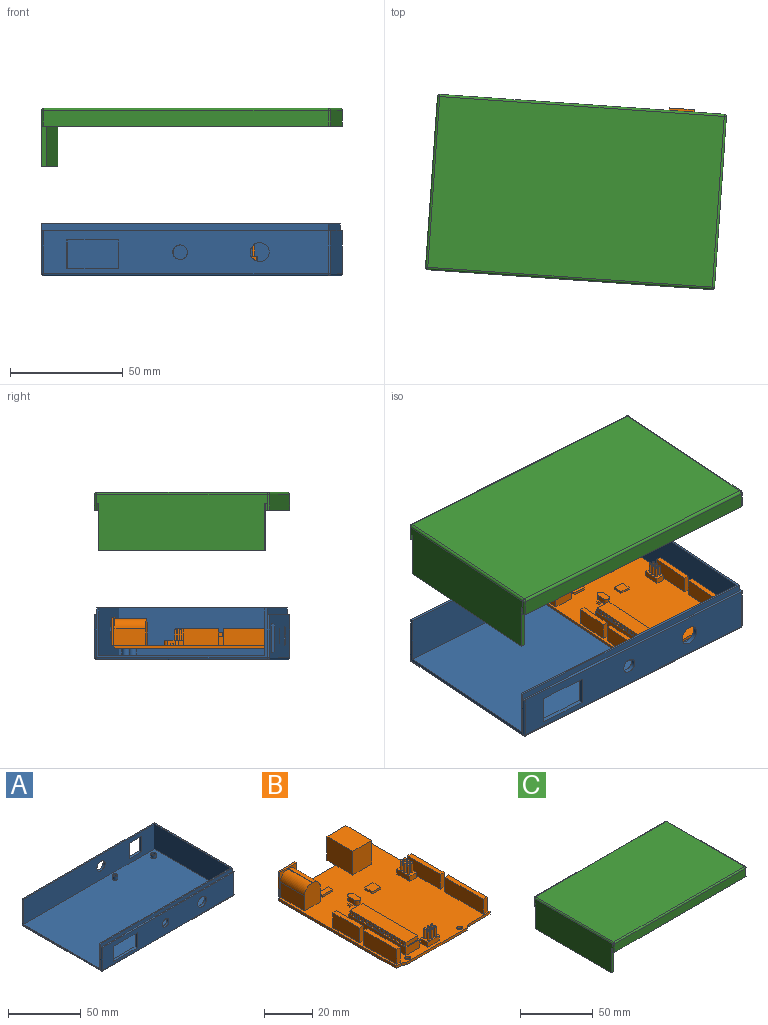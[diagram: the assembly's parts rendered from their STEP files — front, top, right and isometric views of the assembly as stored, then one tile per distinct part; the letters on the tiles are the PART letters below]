
ASSEMBLY  parts=3 mates=4
PART A: 53 faces, bbox 128.7x78x23 mm
  f0: plane 128.7x78mm, normal (0,0,1), area 350.9mm2, adj f2,f3,f7,f8,f10,f33,f34,f41
  f1: plane 126.7x21mm, normal (0,-1,0), area 2453.2mm2, adj f6,f9,f11,f28,f29,f30,f31,f32
  f2: plane 126.7x19mm, normal (0,-1,0), area 2030.7mm2, adj f0,f35,f36,f37,f38,f39,f40,f43
  f3: plane 126.7x19mm, normal (0,1,0), area 2199.8mm2, adj f0,f28,f29,f30,f31,f32,f41,f45
  f4: plane 126.7x76mm, normal (0,0,-1), area 9629.2mm2, adj f44,f45,f49,f50
  f5: plane 126.7x21mm, normal (0,1,0), area 2284.1mm2, adj f6,f9,f11,f34,f35,f36,f37,f38
  f6: plane 126.7x74mm, normal (0,0,1), area 9337.3mm2, adj f1,f5,f11,f13,f17,f21,f25,f34
  f7: plane 127.67x3mm, normal (0,1,0), area 383mm2, adj f0,f9,f33,f34
  f8: plane 127.67x3mm, normal (0,-1,0), area 383mm2, adj f0,f9,f33,f34
  f9: plane 127.67x75.88mm, normal (0,0,1), area 311.1mm2, adj f1,f5,f7,f8,f11,f33,f34
  f10: plane 76x19mm, normal (1,0,0), area 1444mm2, adj f0,f41,f43,f44
  f11: plane 74x21mm, normal (-1,0,0), area 1554mm2, adj f1,f5,f6,f9
  f12: cylinder r=1.25mm len=3mm, axis (0,0,-1), area 23.6mm2, adj f14,f15
  f13: cylinder r=1.75mm len=3.5mm, axis (0,0,-1), area 33mm2, adj f6,f14
  f14: plane 3.5x3.5mm, normal (0,0,1), area 4.7mm2, adj f12,f13
  f15: plane 2.5x2.5mm, normal (0,0,1), area 4.9mm2, adj f12
  f16: cylinder r=1.25mm len=3mm, axis (0,0,-1), area 23.6mm2, adj f18,f19
  f17: cylinder r=1.75mm len=3.5mm, axis (0,0,-1), area 33mm2, adj f6,f18
  f18: plane 3.5x3.5mm, normal (0,0,1), area 4.7mm2, adj f16,f17
  f19: plane 2.5x2.5mm, normal (0,0,1), area 4.9mm2, adj f16
  f20: cylinder r=1.25mm len=3mm, axis (0,0,-1), area 23.6mm2, adj f22,f23
  f21: cylinder r=1.75mm len=3.5mm, axis (0,0,-1), area 33mm2, adj f6,f22
  f22: plane 3.5x3.5mm, normal (0,0,1), area 4.7mm2, adj f20,f21
  f23: plane 2.5x2.5mm, normal (0,0,1), area 4.9mm2, adj f20
  f24: cylinder r=1.25mm len=3mm, axis (0,0,-1), area 23.6mm2, adj f26,f27
  f25: cylinder r=1.75mm len=3.5mm, axis (0,0,-1), area 33mm2, adj f6,f26
  f26: plane 3.5x3.5mm, normal (0,0,1), area 4.7mm2, adj f24,f25
  f27: plane 2.5x2.5mm, normal (0,0,1), area 4.9mm2, adj f24
  f28: plane 13x2mm, normal (-1,0,0), area 26mm2, adj f1,f3,f29,f31
  f29: plane 12.11x2mm, normal (0,0,1), area 24.2mm2, adj f1,f3,f28,f30
  f30: plane 13x2mm, normal (1,0,0), area 26mm2, adj f1,f3,f29,f31
  f31: plane 12.11x2mm, normal (0,0,-1), area 24.2mm2, adj f1,f3,f28,f30
  f32: cylinder r=3.99mm len=7.98mm, axis (0,1,0), area 50.2mm2, adj f1,f3
  f33: plane 75.88x3mm, normal (1,0,0), area 227.6mm2, adj f0,f7,f8,f9
  f34: plane 76x22mm, normal (-1,0,0), area 117.6mm2, adj f0,f1,f5,f6,f7,f8,f9,f46
  f35: plane 12.6x2mm, normal (1,0,0), area 25.2mm2, adj f2,f5,f36,f38
  f36: plane 22.75x2mm, normal (0,0,1), area 45.5mm2, adj f2,f5,f35,f37
  f37: plane 12.6x2mm, normal (-1,0,0), area 25.2mm2, adj f2,f5,f36,f38
  f38: plane 22.75x2mm, normal (0,0,-1), area 45.5mm2, adj f2,f5,f35,f37
  f39: cylinder r=3.25mm len=6.5mm, axis (0,-1,0), area 40.8mm2, adj f2,f5
  f40: cylinder r=4.25mm len=8.5mm, axis (0,-1,0), area 53.4mm2, adj f2,f5
  f41: cylinder r=1mm len=19mm, axis (0,0,-1), area 29.8mm2, adj f0,f3,f10,f42
  f42: sphere r=1mm, area 1.6mm2, adj f41,f44,f45
  f43: cylinder r=1mm len=19mm, axis (0,0,1), area 29.8mm2, adj f0,f2,f10,f47
  f44: cylinder r=1mm len=76mm, axis (0,1,0), area 119.4mm2, adj f4,f10,f42,f47
  f45: cylinder r=1mm len=126.7mm, axis (-1,0,0), area 199mm2, adj f3,f4,f42,f48
  f46: cylinder r=1mm len=19mm, axis (0,0,1), area 29.8mm2, adj f0,f3,f34,f48
  f47: sphere r=1mm, area 1.6mm2, adj f43,f44,f49
  f48: sphere r=1mm, area 1.6mm2, adj f45,f46,f50
  f49: cylinder r=1mm len=126.7mm, axis (1,0,0), area 199mm2, adj f2,f4,f47,f51
  f50: cylinder r=1mm len=76mm, axis (0,1,0), area 119.4mm2, adj f4,f34,f48,f51
  f51: sphere r=1mm, area 1.6mm2, adj f49,f50,f52
  f52: cylinder r=1mm len=19mm, axis (0,0,-1), area 29.8mm2, adj f0,f2,f34,f51
PART B: 244 faces, bbox 55x75.2x13.8 mm
  f0: plane 7x4mm, normal (0,0,1), area 23.3mm2, adj f194,f195,f196,f197,f226,f227,f228,f229
  f1: plane 7.5x4mm, normal (0,0,1), area 25.3mm2, adj f190,f191,f192,f193,f220,f221,f222,f223
  f2: plane 70x55mm, normal (0,0,1), area 3025.5mm2, adj f49,f50,f51,f52,f54,f55,f56,f57
  f3: plane 8.98x8.63mm, normal (0,1,0), area 52mm2, adj f179,f180,f181,f182,f183,f184,f185,f186
  f4: plane 1.5x0.4mm, normal (0,1,0), area 0.6mm2, adj f6,f46,f48,f178
  f5: plane 1.5x0.4mm, normal (0,-1,0), area 0.6mm2, adj f6,f46,f48,f178
  f6: plane 0.75x0.4mm, normal (0,0,1), area 0.3mm2, adj f4,f5,f46,f178
  f7: plane 1.5x0.4mm, normal (0,1,0), area 0.6mm2, adj f9,f46,f48,f177
  f8: plane 1.5x0.4mm, normal (0,-1,0), area 0.6mm2, adj f9,f46,f48,f177
  f9: plane 0.75x0.4mm, normal (0,0,1), area 0.3mm2, adj f7,f8,f46,f177
  f10: plane 1.5x0.4mm, normal (0,1,0), area 0.6mm2, adj f12,f46,f48,f176
  f11: plane 1.5x0.4mm, normal (0,-1,0), area 0.6mm2, adj f12,f46,f48,f176
  f12: plane 0.75x0.4mm, normal (0,0,1), area 0.3mm2, adj f10,f11,f46,f176
  f13: plane 1.5x0.4mm, normal (0,1,0), area 0.6mm2, adj f15,f46,f48,f175
  f14: plane 1.5x0.4mm, normal (0,-1,0), area 0.6mm2, adj f15,f46,f48,f175
  f15: plane 0.75x0.4mm, normal (0,0,1), area 0.3mm2, adj f13,f14,f46,f175
  f16: plane 1.5x0.4mm, normal (0,1,0), area 0.6mm2, adj f18,f46,f48,f174
  f17: plane 1.5x0.4mm, normal (0,-1,0), area 0.6mm2, adj f18,f46,f48,f174
  f18: plane 0.75x0.4mm, normal (0,0,1), area 0.3mm2, adj f16,f17,f46,f174
  f19: plane 1.5x0.4mm, normal (0,1,0), area 0.6mm2, adj f21,f46,f48,f173
  f20: plane 1.5x0.4mm, normal (0,-1,0), area 0.6mm2, adj f21,f46,f48,f173
  f21: plane 0.75x0.4mm, normal (0,0,1), area 0.3mm2, adj f19,f20,f46,f173
  f22: plane 1.5x0.4mm, normal (0,1,0), area 0.6mm2, adj f24,f46,f48,f172
  f23: plane 1.5x0.4mm, normal (0,-1,0), area 0.6mm2, adj f24,f46,f48,f172
  f24: plane 0.75x0.4mm, normal (0,0,1), area 0.3mm2, adj f22,f23,f46,f172
  f25: plane 1.5x0.4mm, normal (0,1,0), area 0.6mm2, adj f27,f46,f48,f171
  f26: plane 1.5x0.4mm, normal (0,-1,0), area 0.6mm2, adj f27,f46,f48,f171
  f27: plane 0.75x0.4mm, normal (0,0,1), area 0.3mm2, adj f25,f26,f46,f171
  f28: plane 1.5x0.4mm, normal (0,1,0), area 0.6mm2, adj f30,f46,f48,f170
  f29: plane 1.5x0.4mm, normal (0,-1,0), area 0.6mm2, adj f30,f46,f48,f170
  f30: plane 0.75x0.4mm, normal (0,0,1), area 0.3mm2, adj f28,f29,f46,f170
  f31: plane 1.5x0.4mm, normal (0,1,0), area 0.6mm2, adj f33,f46,f48,f169
  f32: plane 1.5x0.4mm, normal (0,-1,0), area 0.6mm2, adj f33,f46,f48,f169
  f33: plane 0.75x0.4mm, normal (0,0,1), area 0.3mm2, adj f31,f32,f46,f169
  f34: plane 1.5x0.4mm, normal (0,1,0), area 0.6mm2, adj f36,f46,f48,f168
  f35: plane 1.5x0.4mm, normal (0,-1,0), area 0.6mm2, adj f36,f46,f48,f168
  f36: plane 0.75x0.4mm, normal (0,0,1), area 0.3mm2, adj f34,f35,f46,f168
  f37: plane 1.5x0.4mm, normal (0,1,0), area 0.6mm2, adj f39,f46,f48,f167
  f38: plane 1.5x0.4mm, normal (0,-1,0), area 0.6mm2, adj f39,f46,f48,f167
  f39: plane 0.75x0.4mm, normal (0,0,1), area 0.3mm2, adj f37,f38,f46,f167
  f40: plane 1.5x0.4mm, normal (0,1,0), area 0.6mm2, adj f42,f46,f48,f166
  f41: plane 1.5x0.4mm, normal (0,-1,0), area 0.6mm2, adj f42,f46,f48,f166
  f42: plane 0.75x0.4mm, normal (0,0,1), area 0.3mm2, adj f40,f41,f46,f166
  f43: plane 1.5x0.4mm, normal (0,1,0), area 0.6mm2, adj f45,f46,f48,f165
  f44: plane 1.5x0.4mm, normal (0,-1,0), area 0.6mm2, adj f45,f46,f48,f165
  f45: plane 0.75x0.4mm, normal (0,0,1), area 0.3mm2, adj f43,f44,f46,f165
  f46: plane 32.63x2mm, normal (1,0,0), area 49.5mm2, adj f4,f5,f6,f7,f8,f9,f10,f11
  f47: plane 32.63x2mm, normal (-1,0,0), area 49.5mm2, adj f48,f106,f107,f108,f109,f110,f111,f112
  f48: plane 33.63x7.95mm, normal (0,0,1), area 32.2mm2, adj f4,f5,f7,f8,f10,f11,f13,f14
  f49: plane 33.63x4mm, normal (-1,0,0), area 134.5mm2, adj f2,f48,f50,f52
  f50: plane 7.95x4mm, normal (0,-1,0), area 31.8mm2, adj f2,f48,f49,f51
  f51: plane 33.63x4mm, normal (1,0,0), area 134.5mm2, adj f2,f48,f50,f52
  f52: plane 7.95x4mm, normal (0,1,0), area 31.8mm2, adj f2,f48,f49,f51
  f53: plane 6.98x6.98mm, normal (0,1,0), area 37.5mm2, adj f103,f104
  f54: plane 68.67x1.25mm, normal (1,0,0), area 85.8mm2, adj f2,f55,f58,f95
  f55: plane 55x1.25mm, normal (0,1,0), area 68.8mm2, adj f2,f54,f56,f58,f79,f84
  f56: plane 68.67x1.25mm, normal (-1,0,0), area 85.8mm2, adj f2,f55,f58,f92
  f57: plane 35.3x1.25mm, normal (0,-1,0), area 44.1mm2, adj f2,f58,f93,f94
  f58: plane 70x55mm, normal (0,0,-1), area 3816.6mm2, adj f54,f55,f56,f57,f92,f93,f94,f95
  f59: plane 7.5x2.22mm, normal (0,-1,0), area 16.7mm2, adj f2,f60,f62,f63
  f60: plane 22.58x7.5mm, normal (1,0,0), area 169.3mm2, adj f2,f59,f61,f63
  f61: plane 7.5x2.22mm, normal (0,1,0), area 16.7mm2, adj f2,f60,f62,f63
  f62: plane 22.58x7.5mm, normal (-1,0,0), area 169.3mm2, adj f2,f59,f61,f63
  f63: plane 22.58x2.22mm, normal (0,0,1), area 50.1mm2, adj f59,f60,f61,f62
  f64: plane 19.27x7.5mm, normal (-1,0,0), area 144.5mm2, adj f2,f65,f67,f68
  f65: plane 7.5x2.22mm, normal (0,-1,0), area 16.7mm2, adj f2,f64,f66,f68
  f66: plane 19.27x7.5mm, normal (1,0,0), area 144.5mm2, adj f2,f65,f67,f68
  f67: plane 7.5x2.22mm, normal (0,1,0), area 16.7mm2, adj f2,f64,f66,f68
  f68: plane 19.27x2.22mm, normal (0,0,1), area 42.8mm2, adj f64,f65,f66,f67
  f69: plane 19.1x7.5mm, normal (-1,0,0), area 143.2mm2, adj f2,f70,f72,f73
  f70: plane 7.5x2.22mm, normal (0,-1,0), area 16.7mm2, adj f2,f69,f71,f73
  f71: plane 19.1x7.5mm, normal (1,0,0), area 143.2mm2, adj f2,f70,f72,f73
  f72: plane 7.5x2.22mm, normal (0,1,0), area 16.7mm2, adj f2,f69,f71,f73
  f73: plane 19.1x2.22mm, normal (0,0,1), area 42.4mm2, adj f69,f70,f71,f72
  f74: plane 15.53x7.5mm, normal (1,0,0), area 116.5mm2, adj f2,f75,f77,f78
  f75: plane 7.5x2.22mm, normal (0,1,0), area 16.7mm2, adj f2,f74,f76,f78
  f76: plane 15.53x7.5mm, normal (-1,0,0), area 116.5mm2, adj f2,f75,f77,f78
  f77: plane 7.5x2.22mm, normal (0,-1,0), area 16.7mm2, adj f2,f74,f76,f78
  f78: plane 15.53x2.22mm, normal (0,0,1), area 34.5mm2, adj f74,f75,f76,f77
  f79: plane 9.89x1.2mm, normal (0,0,-1), area 11.7mm2, adj f55,f80,f82,f98,f99,f101,f102
  f80: plane 14.15x7.5mm, normal (-1,0,0), area 106.1mm2, adj f2,f79,f81,f90,f98
  f81: plane 12x9.24mm, normal (0,-1,0), area 102.2mm2, adj f2,f80,f82,f83,f90,f91
  f82: plane 14.15x7.5mm, normal (1,0,0), area 106.1mm2, adj f2,f79,f81,f91,f98
  f83: plane 14.15x0.24mm, normal (0,0,1), area 3.4mm2, adj f81,f90,f91,f98
  f84: plane 11.11x5.16mm, normal (0,0,-1), area 57.3mm2, adj f55,f85,f87,f88
  f85: plane 15.05x12mm, normal (-1,0,0), area 180.6mm2, adj f2,f84,f86,f88,f89
  f86: plane 12x11.11mm, normal (0,-1,0), area 133.3mm2, adj f2,f85,f87,f89
  f87: plane 15.05x12mm, normal (1,0,0), area 180.6mm2, adj f2,f84,f86,f88,f89
  f88: plane 12x11.11mm, normal (0,1,0), area 60.1mm2, adj f84,f85,f87,f89,f179,f180,f181,f182
  f89: plane 15.05x11.11mm, normal (0,0,1), area 167.2mm2, adj f85,f86,f87,f88
  f90: cylinder r=4.5mm len=14.15mm, axis (0,1,0), area 100mm2, adj f80,f81,f83,f98
  f91: cylinder r=4.5mm len=14.15mm, axis (0,-1,0), area 100mm2, adj f81,f82,f83,f98
  f92: plane 2.98x1.25mm, normal (0,-1,0), area 3.7mm2, adj f2,f56,f58,f93
  f93: plane 2.01x1.33mm, normal (-0.55,-0.83,0), area 3mm2, adj f2,f57,f58,f92
  f94: plane 2.01x1.33mm, normal (0.55,-0.83,0), area 3mm2, adj f2,f57,f58,f95
  f95: plane 12.71x1.25mm, normal (0,-1,0), area 15.9mm2, adj f2,f54,f58,f94
  f96: cylinder r=1.25mm len=2.5mm, axis (0,0,1), area 9.8mm2, adj f2,f58
  f97: cylinder r=1.25mm len=2.5mm, axis (0,0,1), area 9.8mm2, adj f2,f58
  f98: plane 12.57x9.89mm, normal (0,-1,0), area 22.1mm2, adj f79,f80,f82,f83,f90,f91,f99,f100
  f99: plane 12.57x1mm, normal (-1,0,0), area 12.6mm2, adj f79,f98,f100,f102
  f100: plane 9.89x1mm, normal (0,0,1), area 9.9mm2, adj f98,f99,f101,f102
  f101: plane 12.57x1mm, normal (1,0,0), area 12.6mm2, adj f79,f98,f100,f102
  f102: plane 12.57x9.89mm, normal (0,1,0), area 86mm2, adj f79,f99,f100,f101,f103
  f103: cylinder r=3.49mm len=12mm, axis (0,1,0), area 263.3mm2, adj f53,f102
  f104: cylinder r=0.5mm len=8mm, axis (0,-1,0), area 25.1mm2, adj f53,f105
  f105: plane 1x1mm, normal (0,1,0), area 0.8mm2, adj f104
  f106: plane 6.95x2mm, normal (0,1,0), area 13.9mm2, adj f46,f47,f48,f108
  f107: plane 6.95x2mm, normal (0,-1,0), area 13.9mm2, adj f46,f47,f48,f108
  f108: plane 32.63x6.95mm, normal (0,0,1), area 226.7mm2, adj f46,f47,f106,f107
  f109: plane 1.5x0.4mm, normal (0,1,0), area 0.6mm2, adj f47,f48,f111,f164
  f110: plane 1.5x0.4mm, normal (0,-1,0), area 0.6mm2, adj f47,f48,f111,f164
  f111: plane 0.75x0.4mm, normal (0,0,1), area 0.3mm2, adj f47,f109,f110,f164
  f112: plane 1.5x0.4mm, normal (0,1,0), area 0.6mm2, adj f47,f48,f114,f163
  f113: plane 1.5x0.4mm, normal (0,-1,0), area 0.6mm2, adj f47,f48,f114,f163
  f114: plane 0.75x0.4mm, normal (0,0,1), area 0.3mm2, adj f47,f112,f113,f163
  f115: plane 1.5x0.4mm, normal (0,1,0), area 0.6mm2, adj f47,f48,f117,f162
  f116: plane 1.5x0.4mm, normal (0,-1,0), area 0.6mm2, adj f47,f48,f117,f162
  f117: plane 0.75x0.4mm, normal (0,0,1), area 0.3mm2, adj f47,f115,f116,f162
  f118: plane 1.5x0.4mm, normal (0,1,0), area 0.6mm2, adj f47,f48,f120,f161
  f119: plane 1.5x0.4mm, normal (0,-1,0), area 0.6mm2, adj f47,f48,f120,f161
  f120: plane 0.75x0.4mm, normal (0,0,1), area 0.3mm2, adj f47,f118,f119,f161
  f121: plane 1.5x0.4mm, normal (0,1,0), area 0.6mm2, adj f47,f48,f123,f160
  f122: plane 1.5x0.4mm, normal (0,-1,0), area 0.6mm2, adj f47,f48,f123,f160
  f123: plane 0.75x0.4mm, normal (0,0,1), area 0.3mm2, adj f47,f121,f122,f160
  f124: plane 1.5x0.4mm, normal (0,1,0), area 0.6mm2, adj f47,f48,f126,f159
  f125: plane 1.5x0.4mm, normal (0,-1,0), area 0.6mm2, adj f47,f48,f126,f159
  f126: plane 0.75x0.4mm, normal (0,0,1), area 0.3mm2, adj f47,f124,f125,f159
  f127: plane 1.5x0.4mm, normal (0,1,0), area 0.6mm2, adj f47,f48,f129,f158
  f128: plane 1.5x0.4mm, normal (0,-1,0), area 0.6mm2, adj f47,f48,f129,f158
  f129: plane 0.75x0.4mm, normal (0,0,1), area 0.3mm2, adj f47,f127,f128,f158
  f130: plane 1.5x0.4mm, normal (0,1,0), area 0.6mm2, adj f47,f48,f132,f157
  f131: plane 1.5x0.4mm, normal (0,-1,0), area 0.6mm2, adj f47,f48,f132,f157
  f132: plane 0.75x0.4mm, normal (0,0,1), area 0.3mm2, adj f47,f130,f131,f157
  f133: plane 1.5x0.4mm, normal (0,1,0), area 0.6mm2, adj f47,f48,f135,f156
  f134: plane 1.5x0.4mm, normal (0,-1,0), area 0.6mm2, adj f47,f48,f135,f156
  f135: plane 0.75x0.4mm, normal (0,0,1), area 0.3mm2, adj f47,f133,f134,f156
  f136: plane 1.5x0.4mm, normal (0,1,0), area 0.6mm2, adj f47,f48,f138,f155
  f137: plane 1.5x0.4mm, normal (0,-1,0), area 0.6mm2, adj f47,f48,f138,f155
  f138: plane 0.75x0.4mm, normal (0,0,1), area 0.3mm2, adj f47,f136,f137,f155
  f139: plane 1.5x0.4mm, normal (0,1,0), area 0.6mm2, adj f47,f48,f141,f154
  f140: plane 1.5x0.4mm, normal (0,-1,0), area 0.6mm2, adj f47,f48,f141,f154
  f141: plane 0.75x0.4mm, normal (0,0,1), area 0.3mm2, adj f47,f139,f140,f154
  f142: plane 1.5x0.4mm, normal (0,1,0), area 0.6mm2, adj f47,f48,f144,f153
  f143: plane 1.5x0.4mm, normal (0,-1,0), area 0.6mm2, adj f47,f48,f144,f153
  f144: plane 0.75x0.4mm, normal (0,0,1), area 0.3mm2, adj f47,f142,f143,f153
  f145: plane 1.5x0.4mm, normal (0,1,0), area 0.6mm2, adj f47,f48,f147,f152
  f146: plane 1.5x0.4mm, normal (0,-1,0), area 0.6mm2, adj f47,f48,f147,f152
  f147: plane 0.75x0.4mm, normal (0,0,1), area 0.3mm2, adj f47,f145,f146,f152
  f148: plane 1.5x0.4mm, normal (0,1,0), area 0.6mm2, adj f47,f48,f150,f151
  f149: plane 1.5x0.4mm, normal (0,-1,0), area 0.6mm2, adj f47,f48,f150,f151
  f150: plane 0.75x0.4mm, normal (0,0,1), area 0.3mm2, adj f47,f148,f149,f151
  f151: plane 1.5x0.75mm, normal (-1,0,0), area 1.1mm2, adj f48,f148,f149,f150
  f152: plane 1.5x0.75mm, normal (-1,0,0), area 1.1mm2, adj f48,f145,f146,f147
  f153: plane 1.5x0.75mm, normal (-1,0,0), area 1.1mm2, adj f48,f142,f143,f144
  f154: plane 1.5x0.75mm, normal (-1,0,0), area 1.1mm2, adj f48,f139,f140,f141
  f155: plane 1.5x0.75mm, normal (-1,0,0), area 1.1mm2, adj f48,f136,f137,f138
  f156: plane 1.5x0.75mm, normal (-1,0,0), area 1.1mm2, adj f48,f133,f134,f135
  f157: plane 1.5x0.75mm, normal (-1,0,0), area 1.1mm2, adj f48,f130,f131,f132
  f158: plane 1.5x0.75mm, normal (-1,0,0), area 1.1mm2, adj f48,f127,f128,f129
  f159: plane 1.5x0.75mm, normal (-1,0,0), area 1.1mm2, adj f48,f124,f125,f126
  f160: plane 1.5x0.75mm, normal (-1,0,0), area 1.1mm2, adj f48,f121,f122,f123
  f161: plane 1.5x0.75mm, normal (-1,0,0), area 1.1mm2, adj f48,f118,f119,f120
  f162: plane 1.5x0.75mm, normal (-1,0,0), area 1.1mm2, adj f48,f115,f116,f117
  f163: plane 1.5x0.75mm, normal (-1,0,0), area 1.1mm2, adj f48,f112,f113,f114
  f164: plane 1.5x0.75mm, normal (-1,0,0), area 1.1mm2, adj f48,f109,f110,f111
  f165: plane 1.5x0.75mm, normal (1,0,0), area 1.1mm2, adj f43,f44,f45,f48
  f166: plane 1.5x0.75mm, normal (1,0,0), area 1.1mm2, adj f40,f41,f42,f48
  f167: plane 1.5x0.75mm, normal (1,0,0), area 1.1mm2, adj f37,f38,f39,f48
  f168: plane 1.5x0.75mm, normal (1,0,0), area 1.1mm2, adj f34,f35,f36,f48
  f169: plane 1.5x0.75mm, normal (1,0,0), area 1.1mm2, adj f31,f32,f33,f48
  f170: plane 1.5x0.75mm, normal (1,0,0), area 1.1mm2, adj f28,f29,f30,f48
  f171: plane 1.5x0.75mm, normal (1,0,0), area 1.1mm2, adj f25,f26,f27,f48
  f172: plane 1.5x0.75mm, normal (1,0,0), area 1.1mm2, adj f22,f23,f24,f48
  f173: plane 1.5x0.75mm, normal (1,0,0), area 1.1mm2, adj f19,f20,f21,f48
  f174: plane 1.5x0.75mm, normal (1,0,0), area 1.1mm2, adj f16,f17,f18,f48
  f175: plane 1.5x0.75mm, normal (1,0,0), area 1.1mm2, adj f13,f14,f15,f48
  f176: plane 1.5x0.75mm, normal (1,0,0), area 1.1mm2, adj f10,f11,f12,f48
  f177: plane 1.5x0.75mm, normal (1,0,0), area 1.1mm2, adj f7,f8,f9,f48
  f178: plane 1.5x0.75mm, normal (1,0,0), area 1.1mm2, adj f4,f5,f6,f48
  f179: plane 10x6.73mm, normal (1,0,0), area 67.3mm2, adj f3,f88,f180,f184
  f180: plane 10x8.63mm, normal (0,0,1), area 86.3mm2, adj f3,f88,f179,f181
  f181: plane 10x6.73mm, normal (-1,0,0), area 67.3mm2, adj f3,f88,f180,f182
  f182: plane 10x2.24mm, normal (-0.76,0,-0.65), area 29.4mm2, adj f3,f88,f181,f183
  f183: plane 10x4.83mm, normal (0,0,-1), area 48.3mm2, adj f3,f88,f182,f184
  f184: plane 10x2.24mm, normal (0.76,0,-0.65), area 29.4mm2, adj f3,f88,f179,f183
  f185: plane 8x3.45mm, normal (-1,0,0), area 27.6mm2, adj f3,f186,f188,f189
  f186: plane 8x6.13mm, normal (0,0,1), area 49mm2, adj f3,f185,f187,f189
  f187: plane 8x3.45mm, normal (1,0,0), area 27.6mm2, adj f3,f186,f188,f189
  f188: plane 8x6.13mm, normal (0,0,-1), area 49mm2, adj f3,f185,f187,f189
  f189: plane 6.13x3.45mm, normal (0,1,0), area 21.2mm2, adj f185,f186,f187,f188
  f190: plane 7.5x2.5mm, normal (-1,0,0), area 18.7mm2, adj f1,f2,f191,f193
  f191: plane 4x2.5mm, normal (0,-1,0), area 10mm2, adj f1,f2,f190,f192
  f192: plane 7.5x2.5mm, normal (1,0,0), area 18.7mm2, adj f1,f2,f191,f193
  f193: plane 4x2.5mm, normal (0,1,0), area 10mm2, adj f1,f2,f190,f192
  f194: plane 4x2.5mm, normal (-1,0,0), area 10mm2, adj f0,f2,f195,f197
  f195: plane 7x2.5mm, normal (0,-1,0), area 17.5mm2, adj f0,f2,f194,f196
  f196: plane 4x2.5mm, normal (1,0,0), area 10mm2, adj f0,f2,f195,f197
  f197: plane 7x2.5mm, normal (0,1,0), area 17.5mm2, adj f0,f2,f194,f196
  f198: plane 3.5x2.5mm, normal (-1,0,0), area 8.8mm2, adj f2,f200,f201,f203
  f199: plane 3.5x2.5mm, normal (1,0,0), area 8.8mm2, adj f2,f200,f202,f204
  f200: plane 6.5x3mm, normal (0,0,1), area 17.6mm2, adj f198,f199,f201,f202,f203,f204
  f201: cylinder r=1.5mm len=2.5mm, axis (0,0,-1), area 5.9mm2, adj f2,f198,f200,f202
  f202: cylinder r=1.5mm len=2.5mm, axis (0,0,-1), area 5.9mm2, adj f2,f199,f200,f201
  f203: cylinder r=1.5mm len=2.5mm, axis (0,0,-1), area 5.9mm2, adj f2,f198,f200,f204
  f204: cylinder r=1.5mm len=2.5mm, axis (0,0,-1), area 5.9mm2, adj f2,f199,f200,f203
  f205: plane 2.66x1mm, normal (-1,0,0), area 2.7mm2, adj f2,f206,f208,f209
  f206: plane 5.95x1mm, normal (0,-1,0), area 6mm2, adj f2,f205,f207,f209
  f207: plane 2.66x1mm, normal (1,0,0), area 2.7mm2, adj f2,f206,f208,f209
  f208: plane 5.95x1mm, normal (0,1,0), area 6mm2, adj f2,f205,f207,f209
  f209: plane 5.95x2.66mm, normal (0,0,1), area 15.9mm2, adj f205,f206,f207,f208
  f210: plane 1.1x1mm, normal (-1,0,0), area 1.1mm2, adj f2,f211,f213,f214
  f211: plane 1.57x1mm, normal (0,-1,0), area 1.6mm2, adj f2,f210,f212,f214
  f212: plane 1.1x1mm, normal (1,0,0), area 1.1mm2, adj f2,f211,f213,f214
  f213: plane 1.57x1mm, normal (0,1,0), area 1.6mm2, adj f2,f210,f212,f214
  f214: plane 1.57x1.1mm, normal (0,0,1), area 1.7mm2, adj f210,f211,f212,f213
  f215: plane 4.54x1mm, normal (-1,0,0), area 4.5mm2, adj f2,f216,f218,f219
  f216: plane 4.86x1mm, normal (0,-1,0), area 4.9mm2, adj f2,f215,f217,f219
  f217: plane 4.54x1mm, normal (1,0,0), area 4.5mm2, adj f2,f216,f218,f219
  f218: plane 4.86x1mm, normal (0,1,0), area 4.9mm2, adj f2,f215,f217,f219
  f219: plane 4.86x4.54mm, normal (0,0,1), area 22.1mm2, adj f215,f216,f217,f218
  f220: cylinder r=0.5mm len=4.5mm, axis (0,0,-1), area 14.1mm2, adj f1,f237
  f221: cylinder r=0.5mm len=4.5mm, axis (0,0,-1), area 14.1mm2, adj f1,f238
  f222: cylinder r=0.5mm len=4.5mm, axis (0,0,-1), area 14.1mm2, adj f1,f235
  f223: cylinder r=0.5mm len=4.5mm, axis (0,0,-1), area 14.1mm2, adj f1,f232
  f224: cylinder r=0.5mm len=4.5mm, axis (0,0,-1), area 14.1mm2, adj f1,f233
  f225: cylinder r=0.5mm len=4.5mm, axis (0,0,-1), area 14.1mm2, adj f1,f234
  f226: cylinder r=0.5mm len=4.5mm, axis (0,0,-1), area 14.1mm2, adj f0,f239
  f227: cylinder r=0.5mm len=4.5mm, axis (0,0,-1), area 14.1mm2, adj f0,f236
  f228: cylinder r=0.5mm len=4.5mm, axis (0,0,-1), area 14.1mm2, adj f0,f242
  f229: cylinder r=0.5mm len=4.5mm, axis (0,0,-1), area 14.1mm2, adj f0,f241
  f230: cylinder r=0.5mm len=4.5mm, axis (0,0,-1), area 14.1mm2, adj f0,f240
  f231: cylinder r=0.5mm len=4.5mm, axis (0,0,-1), area 14.1mm2, adj f0,f243
  f232: sphere r=0.5mm, area 1.6mm2, adj f223
  f233: sphere r=0.5mm, area 1.6mm2, adj f224
  f234: sphere r=0.5mm, area 1.6mm2, adj f225
  f235: sphere r=0.5mm, area 1.6mm2, adj f222
  f236: sphere r=0.5mm, area 1.6mm2, adj f227
  f237: sphere r=0.5mm, area 1.6mm2, adj f220
  f238: sphere r=0.5mm, area 1.6mm2, adj f221
  f239: sphere r=0.5mm, area 1.6mm2, adj f226
  f240: sphere r=0.5mm, area 1.6mm2, adj f230
  f241: sphere r=0.5mm, area 1.6mm2, adj f229
  f242: sphere r=0.5mm, area 1.6mm2, adj f228
  f243: sphere r=0.5mm, area 1.6mm2, adj f231
PART C: 30 faces, bbox 128.7x78x25.9 mm
  f0: plane 124.68x74mm, normal (0,0,-1), area 9226.1mm2, adj f8,f9,f12,f16
  f1: plane 128.7x78mm, normal (0,0,-1), area 350.9mm2, adj f2,f3,f5,f6,f10,f11,f13,f18
  f2: plane 126.7x7mm, normal (0,1,0), area 886.9mm2, adj f1,f18,f20,f21
  f3: plane 126.7x7mm, normal (0,-1,0), area 886.9mm2, adj f1,f23,f27,f29
  f4: plane 126.7x76mm, normal (0,0,1), area 9629.2mm2, adj f21,f22,f26,f27
  f5: plane 127.67x3mm, normal (0,-1,0), area 383mm2, adj f1,f7,f11,f13
  f6: plane 127.67x3mm, normal (0,1,0), area 383mm2, adj f1,f7,f11,f13
  f7: plane 127.67x75.88mm, normal (0,0,-1), area 311.1mm2, adj f5,f6,f8,f9,f11,f12,f13,f14
  f8: plane 124.68x3mm, normal (0,-1,0), area 374mm2, adj f0,f7,f12,f16
  f9: plane 124.68x3mm, normal (0,1,0), area 374mm2, adj f0,f7,f12,f16
  f10: plane 76x7mm, normal (1,0,0), area 532mm2, adj f1,f18,f22,f23
  f11: plane 75.88x3mm, normal (-1,0,0), area 227.6mm2, adj f1,f5,f6,f7
  f12: plane 74x3mm, normal (-1,0,0), area 222mm2, adj f0,f7,f8,f9
  f13: plane 76x24.88mm, normal (-1,0,0), area 1849.5mm2, adj f1,f5,f6,f7,f14,f15,f17,f20
  f14: plane 20.88x2.02mm, normal (0,1,0), area 42.3mm2, adj f7,f13,f16,f17
  f15: plane 20.88x2.02mm, normal (0,-1,0), area 42.3mm2, adj f7,f13,f16,f17
  f16: plane 74x23.88mm, normal (1,0,0), area 1767.1mm2, adj f0,f8,f9,f14,f15,f17
  f17: plane 74x2.02mm, normal (0,0,-1), area 149.7mm2, adj f13,f14,f15,f16
  f18: cylinder r=1mm len=7mm, axis (0,0,1), area 11mm2, adj f1,f2,f10,f19
  f19: sphere r=1mm, area 1.6mm2, adj f18,f21,f22
  f20: cylinder r=1mm len=7mm, axis (0,0,1), area 11mm2, adj f1,f2,f13,f24
  f21: cylinder r=1mm len=126.7mm, axis (1,0,0), area 199mm2, adj f2,f4,f19,f24
  f22: cylinder r=1mm len=76mm, axis (0,-1,0), area 119.4mm2, adj f4,f10,f19,f25
  f23: cylinder r=1mm len=7mm, axis (0,0,-1), area 11mm2, adj f1,f3,f10,f25
  f24: sphere r=1mm, area 1.6mm2, adj f20,f21,f26
  f25: sphere r=1mm, area 1.6mm2, adj f22,f23,f27
  f26: cylinder r=1mm len=76mm, axis (0,-1,0), area 119.4mm2, adj f4,f13,f24,f28
  f27: cylinder r=1mm len=126.7mm, axis (-1,0,0), area 199mm2, adj f3,f4,f25,f28
  f28: sphere r=1mm, area 1.6mm2, adj f26,f27,f29
  f29: cylinder r=1mm len=7mm, axis (0,0,-1), area 11mm2, adj f1,f3,f13,f28
PLACE A rot(axis=(0,0,-1),4deg) t=(-40.8,-55.1,23.35)mm fixed
PLACE B rot(axis=(0,0,-1),4deg) t=(-40.8,-55.1,23.35)mm
PLACE C rot(axis=(0,0,-1),4deg) t=(-40.8,-55.1,69.77)mm
MATE planar C.f11 <-> A.f33  axis (-1,0.07,0) through (-10.41,-57.19,86.27)mm
MATE cylindrical A.f16 <-> B.f96  axis (0,0,1) through (-63.06,-86.62,23.35)mm
MATE planar C.f6 <-> A.f8  axis (0.07,1,0) through (-76.73,-90.58,86.27)mm
MATE planar B.f58 <-> A.f12  axis (0,0,-1) through (-40.84,-54.8,23.35)mm
